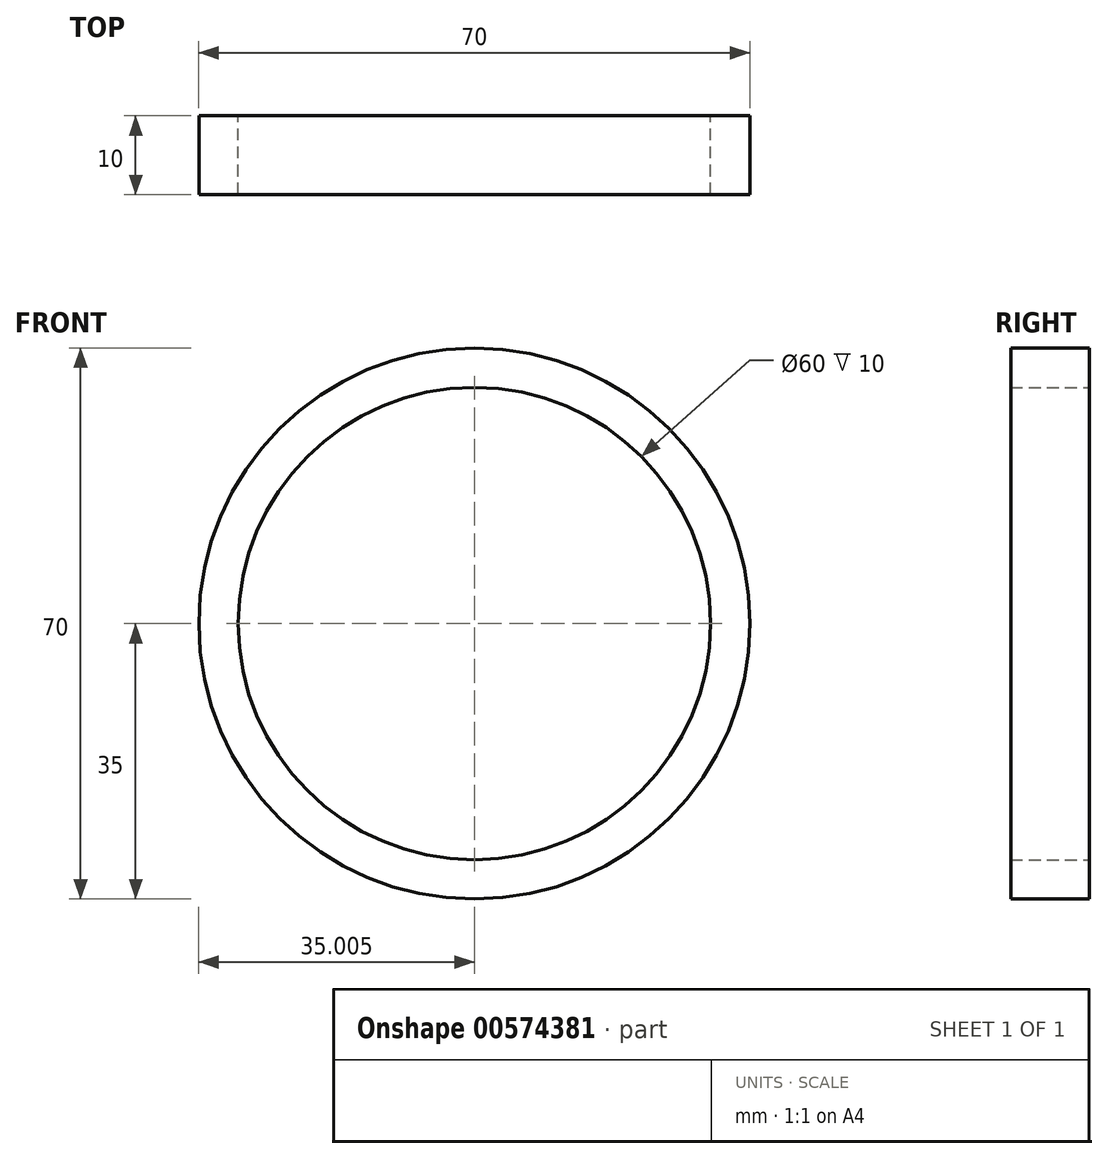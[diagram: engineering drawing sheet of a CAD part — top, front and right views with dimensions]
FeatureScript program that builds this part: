
annotation { "Feature Type Name" : "Feature", "Feature Type Description" : "" }
export const myFeature = defineFeature(function(context is Context, id is Id, definition is map)
    precondition{}
    {
        {
            var Q0;
            Q0=qCreatedBy(makeId("Front.planeOp"),FACE);
            var sketch = newSketch(context, id + "F0", { "sketchPlane" : qUnion([Q0])});
            skCircle(sketch, "E0", {"center": v(-253.62, 0) * mm, "radius": 30 * mm});
            skCircle(sketch, "E1", {"center": v(-253.62, 0) * mm, "radius": 35 * mm});
            skSolve(sketch);
        }
        {
            var Q0;
            Q0=makeQuery(id+"F0.imprint","IMPRINT",FACE,{"disambiguationData":[TD([[makeQuery(id+"F0.imprint","IMPRINT",EDGE,{"derivedFrom":sQuery(id+"F0.wireOp",EDGE,"E0")}),-1.0]])]});
            extrude(context, id + "F1", {"entities" : qUnion([Q0]), "endBound" : BoundingType.SYMMETRIC, "depth" : 10 * mm, "offsetDistance" : 25 * mm});
        }
    });
